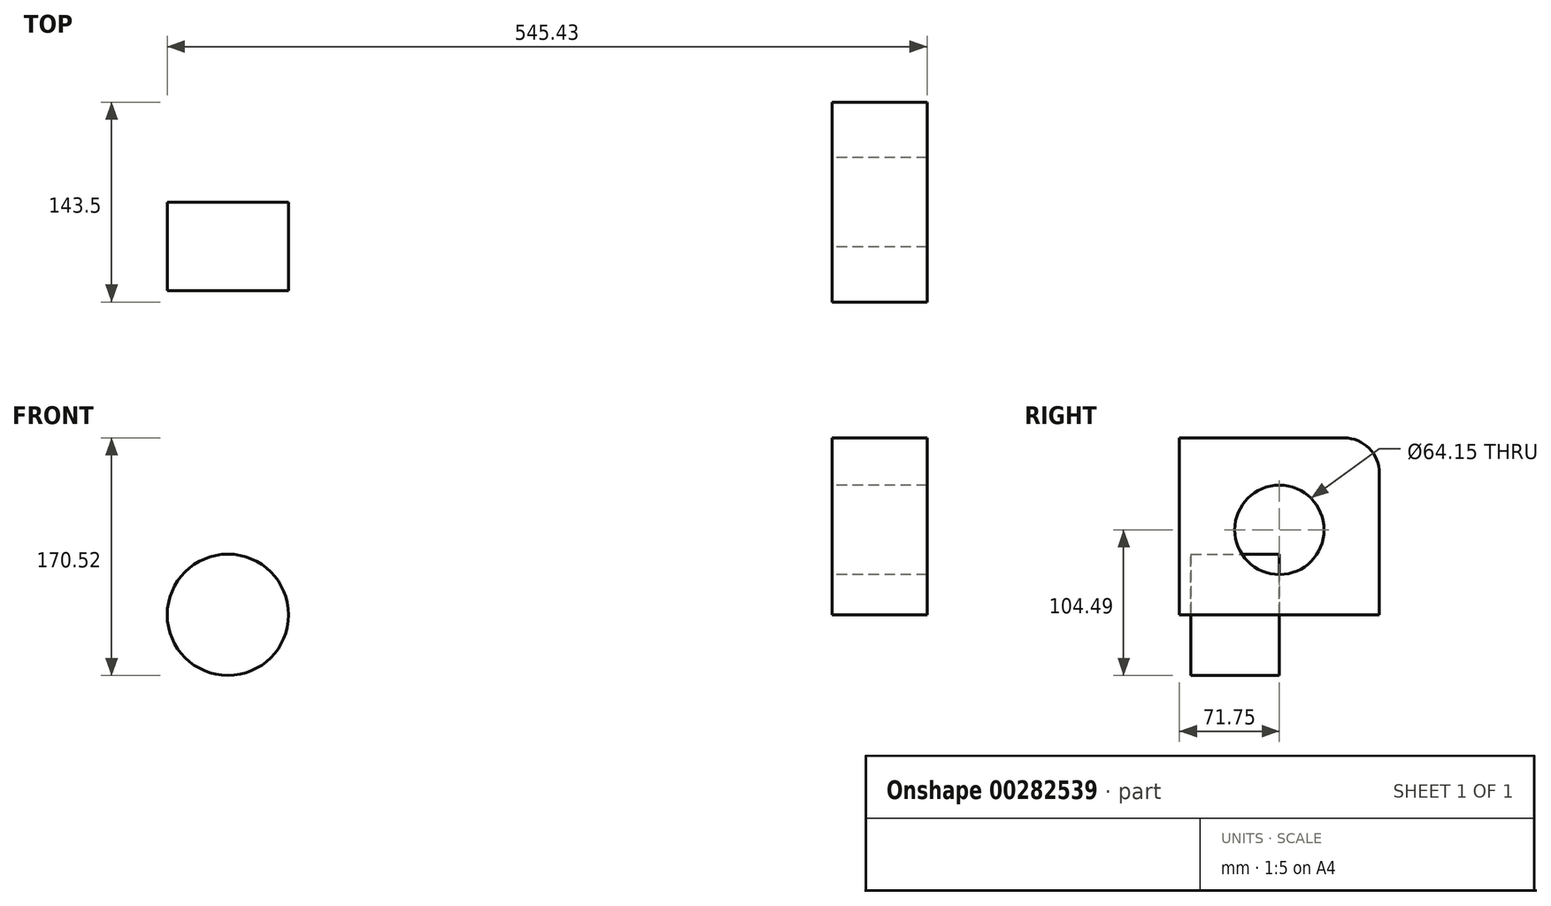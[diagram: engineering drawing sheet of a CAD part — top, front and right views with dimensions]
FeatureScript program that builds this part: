
annotation { "Feature Type Name" : "Feature", "Feature Type Description" : "" }
export const myFeature = defineFeature(function(context is Context, id is Id, definition is map)
    precondition{}
    {
        {
            var Q0;
            Q0=qCreatedBy(makeId("Top.planeOp"),FACE);
            var sketch = newSketch(context, id + "F0", { "sketchPlane" : qUnion([Q0])});
            skLineSegment(sketch, "E0.bottom", {"start": v(34.15, 71.76) * mm, "end": v(-34.15, 71.76) * mm});
            skLineSegment(sketch, "E0.top", {"start": v(34.15, -71.76) * mm, "end": v(-34.15, -71.76) * mm});
            skLineSegment(sketch, "E0.left", {"start": v(34.15, 71.76) * mm, "end": v(34.15, -71.76) * mm});
            skLineSegment(sketch, "E0.right", {"start": v(-34.15, 71.76) * mm, "end": v(-34.15, -71.76) * mm});
            skPoint(sketch, "E0.middle", {"position": v(0, 0) * mm});
            skSolve(sketch);
        }
        {
            var Q0;
            Q0 = qSketchRegion(id + "F0", true);
            extrude(context, id + "F1", {"entities" : qUnion([Q0]), "depth" : 127 * mm});
        }
        {
            var Q0;
            Q0=makeQuery(id+"F1.opExtrude","CAP_EDGE",EDGE,{"disambiguationData":[OSD([sQuery(id+"F0.wireOp",EDGE,"E0.bottom")])],"isStart":false});
            fillet(context, id + "F2", {"entities" : qUnion([Q0]), "radius" : 25.4 * mm, "tangentPropagation" : true, "allowEdgeOverflow" : false});
        }
        {
            var Q0;
            Q0=makeQuery(id+"F1.opExtrude","SWEPT_FACE",FACE,{"disambiguationData":[OSD([sQuery(id+"F0.wireOp",EDGE,"E0.right")])]});
            var sketch = newSketch(context, id + "F3", { "sketchPlane" : qUnion([Q0])});
            skCircle(sketch, "E1", {"center": v(0, 60.97) * mm, "radius": 32.08 * mm});
            skPoint(sketch, "E1.centerSnap0", {"position": v(0, 0) * mm});
            skSolve(sketch);
        }
        {
            var Q0;
            Q0=makeQuery(id+"F3.imprint","IMPRINT",FACE,{"disambiguationData":[TD([[makeQuery(id+"F3.imprint","IMPRINT",EDGE,{"derivedFrom":sQuery(id+"F3.wireOp",EDGE,"E1")}),1.0]])]});
            var Q1;
            Q1=sQuery(id+"F3.wireOp",EDGE,"E1");
            extrude(context, id + "F4", {"entities" : qUnion([Q0]), "operationType" : NewBodyOperationType.REMOVE, "surfaceEntities" : qUnion([Q1]), "endBound" : BoundingType.THROUGH_ALL, "oppositeDirection" : true, "depth" : 25.4 * mm});
        }
        {
            var Q0;
            Q0=qCreatedBy(makeId("Front.planeOp"),FACE);
            var sketch = newSketch(context, id + "F5", { "sketchPlane" : qUnion([Q0])});
            skCircle(sketch, "E2", {"center": v(-467.76, 0) * mm, "radius": 43.52 * mm});
            skSolve(sketch);
        }
        {
            var Q0;
            Q0=makeQuery(id+"F5.imprint","IMPRINT",FACE,{"disambiguationData":[TD([[makeQuery(id+"F5.imprint","IMPRINT",EDGE,{"derivedFrom":sQuery(id+"F5.wireOp",EDGE,"E2")}),1.0]])]});
            extrude(context, id + "F6", {"entities" : qUnion([Q0]), "depth" : 63.5 * mm});
        }
    });
